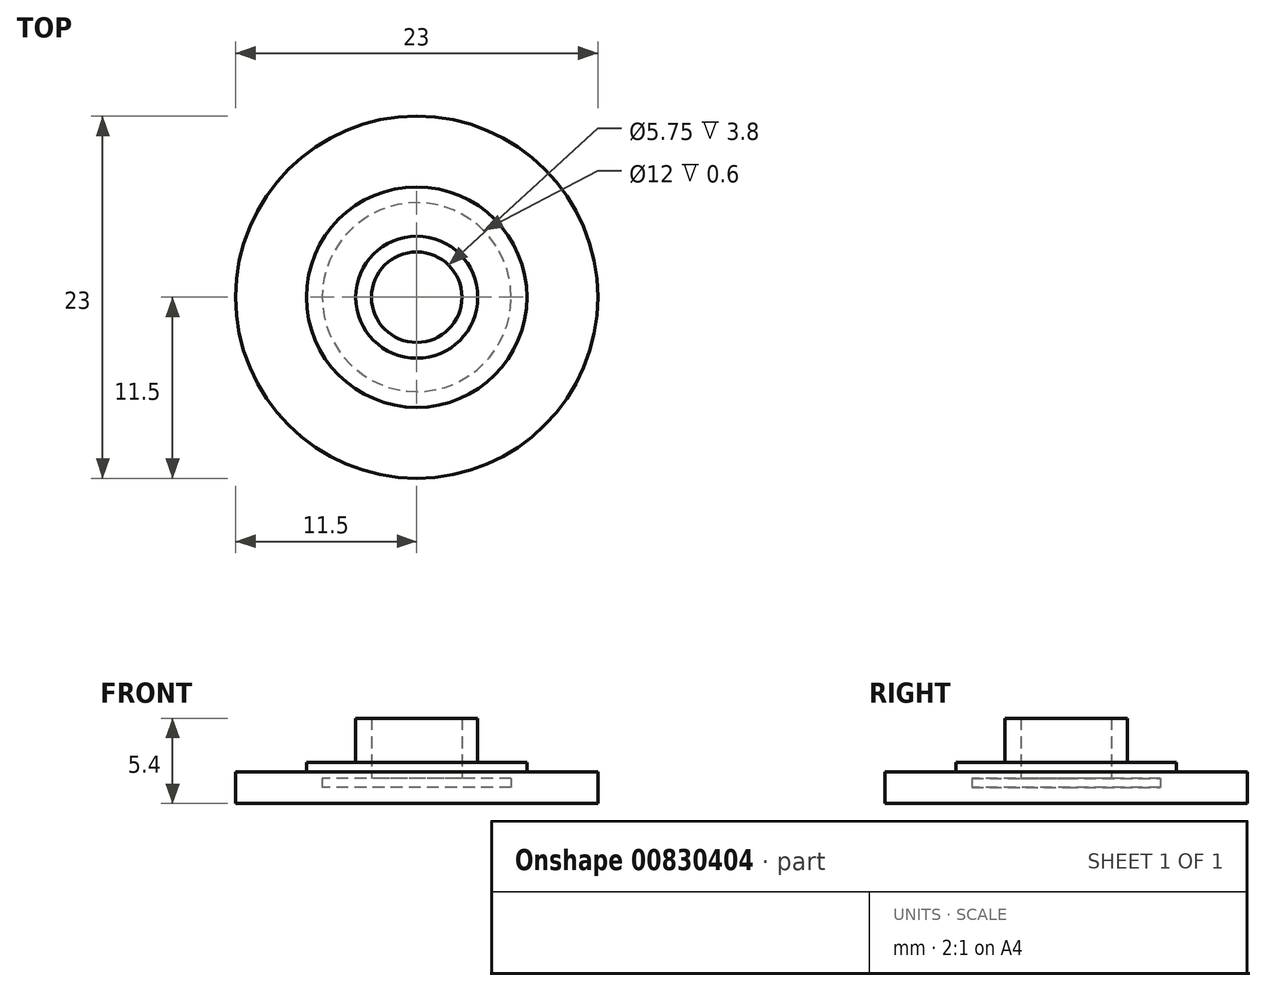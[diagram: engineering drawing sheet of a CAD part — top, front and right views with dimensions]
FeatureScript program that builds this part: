
annotation { "Feature Type Name" : "Feature", "Feature Type Description" : "" }
export const myFeature = defineFeature(function(context is Context, id is Id, definition is map)
    precondition{}
    {
        {
            var Q0;
            Q0=qCreatedBy(makeId("Top.planeOp"),FACE);
            var sketch = newSketch(context, id + "F0", { "sketchPlane" : qUnion([Q0])});
            skCircle(sketch, "E0", {"center": v(0, 0) * mm, "radius": 3.88 * mm});
            skCircle(sketch, "E1", {"center": v(0, 0) * mm, "radius": 7 * mm});
            skCircle(sketch, "E2", {"center": v(0, 0) * mm, "radius": 11.5 * mm});
            skSolve(sketch);
        }
        {
            var Q0;
            Q0=makeQuery(id+"F0.imprint","IMPRINT",FACE,{"disambiguationData":[TD([[makeQuery(id+"F0.imprint","IMPRINT",EDGE,{"derivedFrom":sQuery(id+"F0.wireOp",EDGE,"E0")}),1.0]])]});
            extrude(context, id + "F1", {"entities" : qUnion([Q0]), "depth" : 3.4 * mm, "offsetDistance" : 25 * mm});
        }
        {
            var Q0;
            Q0=makeQuery(id+"F0.imprint","IMPRINT",FACE,{"disambiguationData":[TD([[makeQuery(id+"F0.imprint","IMPRINT",EDGE,{"derivedFrom":sQuery(id+"F0.wireOp",EDGE,"E0")}),-1.0]])]});
            extrude(context, id + "F2", {"entities" : qUnion([Q0]), "operationType" : NewBodyOperationType.ADD, "depth" : 0.6 * mm, "offsetDistance" : 25 * mm});
        }
        {
            var Q0;
            Q0=makeQuery(id+"F0.imprint","IMPRINT",FACE,{"disambiguationData":[TD([[makeQuery(id+"F0.imprint","IMPRINT",EDGE,{"derivedFrom":sQuery(id+"F0.wireOp",EDGE,"E0")}),1.0]])]});
            var Q1;
            Q1=makeQuery(id+"F0.imprint","IMPRINT",FACE,{"disambiguationData":[TD([[makeQuery(id+"F0.imprint","IMPRINT",EDGE,{"derivedFrom":sQuery(id+"F0.wireOp",EDGE,"E0")}),-1.0]])]});
            var Q2;
            Q2=makeQuery(id+"F0.imprint","IMPRINT",FACE,{"disambiguationData":[TD([[makeQuery(id+"F0.imprint","IMPRINT",EDGE,{"derivedFrom":sQuery(id+"F0.wireOp",EDGE,"E1")}),-1.0]])]});
            extrude(context, id + "F3", {"entities" : qUnion([Q0, Q1, Q2]), "operationType" : NewBodyOperationType.ADD, "oppositeDirection" : true, "depth" : 2 * mm, "offsetDistance" : 25 * mm});
        }
        {
            var Q0;
            Q0=makeQuery(id+"F1.opExtrude","CAP_FACE",FACE,{"disambiguationData":[OSD([sQuery(id+"F0.wireOp",EDGE,"E0")])],"isStart":false});
            shell(context, id + "F4", {"entities" : qUnion([Q0]), "thickness" : 1 * mm});
        }
    });
